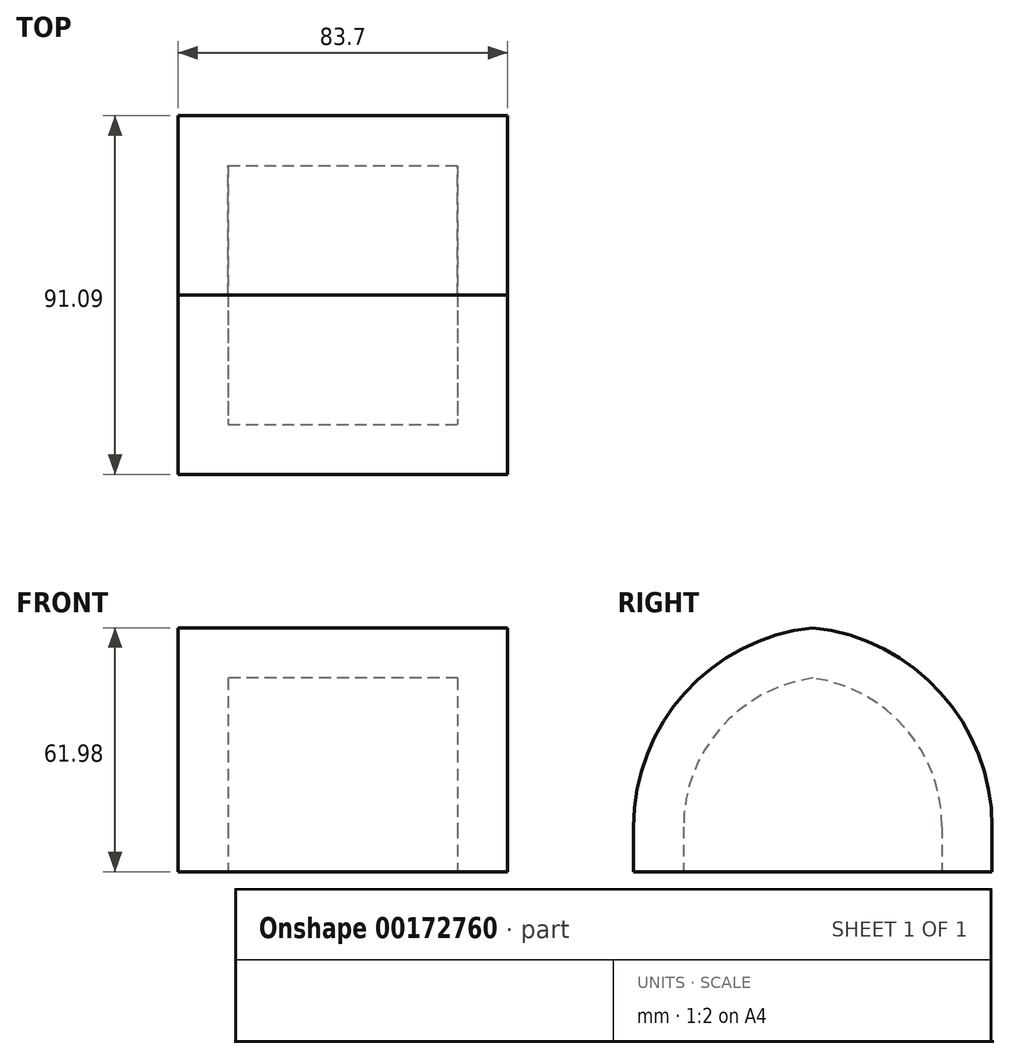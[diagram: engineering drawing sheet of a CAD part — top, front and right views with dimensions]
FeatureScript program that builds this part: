
annotation { "Feature Type Name" : "Feature", "Feature Type Description" : "" }
export const myFeature = defineFeature(function(context is Context, id is Id, definition is map)
    precondition{}
    {
        {
            var Q0;
            Q0=qCreatedBy(makeId("Top.planeOp"),FACE);
            var sketch = newSketch(context, id + "F0", { "sketchPlane" : qUnion([Q0])});
            skLineSegment(sketch, "E0.bottom", {"start": v(-30, 14.95) * mm, "end": v(53.7, 14.95) * mm});
            skLineSegment(sketch, "E0.top", {"start": v(-30, -30.6) * mm, "end": v(53.7, -30.6) * mm});
            skLineSegment(sketch, "E0.left", {"start": v(-30, 14.95) * mm, "end": v(-30, -30.6) * mm});
            skLineSegment(sketch, "E0.right", {"start": v(53.7, 14.95) * mm, "end": v(53.7, -30.6) * mm});
            skSolve(sketch);
        }
        {
            var Q0;
            Q0 = qSketchRegion(id + "F0", true);
            extrude(context, id + "F1", {"entities" : qUnion([Q0]), "depth" : 61.98 * mm});
        }
        {
            var Q0;
            Q0=makeQuery(id+"F1.opExtrude","CAP_EDGE",EDGE,{"disambiguationData":[OSD([sQuery(id+"F0.wireOp",EDGE,"E0.top")])],"isStart":false});
            fillet(context, id + "F2", {"entities" : qUnion([Q0]), "radius" : 50.8 * mm, "tangentPropagation" : true, "allowEdgeOverflow" : false});
        }
        {
            var Q0;
            Q0=makeQuery(id+"F1.opExtrude","SWEPT_FACE",FACE,{"disambiguationData":[OSD([sQuery(id+"F0.wireOp",EDGE,"E0.bottom")])]});
            var Q1;
            Q1=makeQuery(id+"F1.opExtrude","CAP_FACE",FACE,{"disambiguationData":[OSD([sQuery(id+"F0.wireOp",EDGE,"E0.bottom"),sQuery(id+"F0.wireOp",EDGE,"E0.top"),sQuery(id+"F0.wireOp",EDGE,"E0.left"),sQuery(id+"F0.wireOp",EDGE,"E0.right")])],"isStart":true});
            shell(context, id + "F3", {"entities" : qUnion([Q0, Q1]), "thickness" : 12.7 * mm});
        }
        {
            var Q0;
            Q0=makeQuery(id+"F1.opExtrude","SWEPT_BODY",BODY,{"disambiguationData":[OSD([sQuery(id+"F0.wireOp",EDGE,"E0.bottom"),sQuery(id+"F0.wireOp",EDGE,"E0.top"),sQuery(id+"F0.wireOp",EDGE,"E0.left"),sQuery(id+"F0.wireOp",EDGE,"E0.right")])]});
            var Q1;
            Q1=makeQuery(id+"F1.opExtrude","SWEPT_FACE",FACE,{"disambiguationData":[OSD([sQuery(id+"F0.wireOp",EDGE,"E0.bottom")])]});
            mirror(context, id + "F4", {"operationType" : NewBodyOperationType.ADD, "entities" : qUnion([Q0]), "mirrorPlane" : qUnion([Q1])});
        }
    });
